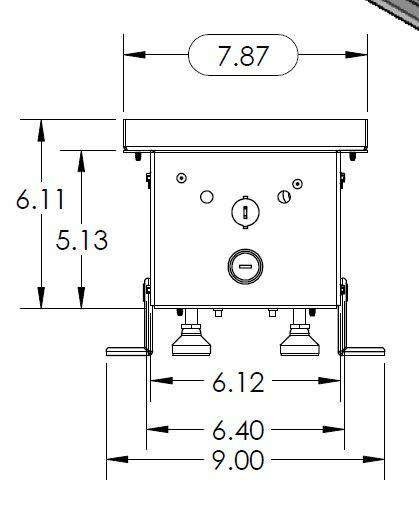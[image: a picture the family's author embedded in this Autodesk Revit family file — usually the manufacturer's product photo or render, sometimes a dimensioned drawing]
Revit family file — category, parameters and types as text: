
# Revit family: Convection_Heater-Berko-THX
name_source: partatom
category: Mechanical Equipment
revit_build: Autodesk Revit 2017 (Build: 20160225_1515(x64)
units: mm (PartAtom-declared; Revit-internal decimal feet)

## family parameters
Cut with Voids When Loaded = No
Host = Face
OmniClass Number = 23.75.70.17.14
OmniClass Title = Convectors
Part Type = Normal
Room Calculation Point = No
Round Connector Dimension = Use Diameter
Shared = No

## types (16) — shared parameters
Amps = 1 A
Apparent Load = 0 VA
Casing = Metal - Berko - Paint - Aluminum
Default Elevation = 3"
Description = THX Trench Heater
Frequency = 60 Hz
Height = 6"
Manufacturer = Berko
Number of Poles = 1
Phase = 2
Power Factor = 1
Product Name = THX Trench Heater
Product Page URL = https://www.marleymep.com
Surface Mount = No
URL = http://www.marleymep.com
Width = 3 5/8"

## per-type parameters (varying)
| type | Length | Length Constraint | Material | Model | Voltage | Watts |
| THX 2' 02188 208V | 2' - 0" | 2' - 4" |  | THX 2' 02188 | 208 V | 400 W |
| THX 3' 03188 208V | 3' - 0" | 3' - 0" |  | THX 3' 03188 | 208 V | 564 W |
| THX 4' 04188 208V | 4' - 0" | 4' - 0" |  | THX 4' 04188 | 208 V | 752 W |
| THX 5' 05188 208V | 5' - 0" | 5' - 0" |  | THX 5' 05188 | 208 V | 940 W |
| THX 2' 02250 208V | 2' - 0" | 2' - 4" |  | THX 2' 02250 | 208 V | 500 W |
| THX 3' 03250 208V | 3' - 0" | 3' - 0" | Metal - Berko - Paint - Aluminum | THX 3' 03250 | 208 V | 750 W |
| THX 4' 04250 208V | 4' - 0" | 4' - 0" |  | THX 4' 04250 | 208 V | 1000 W |
| THX 5' 05250 208V | 5' - 0" | 5' - 0" |  | THX 5' 05250 | 208 V | 1250 W |
| THX 2' 02188 277V | 2' - 0" | 2' - 4" |  | THX 2' 02188 | 277 V | 400 W |
| THX 2' 02250 277V | 2' - 0" | 2' - 4" |  | THX 2' 02250 | 277 V | 500 W |
| THX 3' 03188 277V | 3' - 0" | 3' - 0" |  | THX 3' 03188 | 277 V | 564 W |
| THX 3' 03250 277V | 3' - 0" | 3' - 0" | Metal - Berko - Paint - Aluminum | THX 3' 03250 | 277 V | 750 W |
| THX 4' 04188 277V | 4' - 0" | 4' - 0" |  | THX 4' 04188 | 277 V | 752 W |
| THX 4' 04250 277V | 4' - 0" | 4' - 0" |  | THX 4' 04250 | 277 V | 1000 W |
| THX 5' 05188 277V | 5' - 0" | 5' - 0" |  | THX 5' 05188 | 277 V | 940 W |
| THX 5' 05250 277V | 5' - 0" | 5' - 0" |  | THX 5' 05250 | 277 V | 1250 W |

## geometry (parser evidence)
native form markers: Blend x2, Sweep x1
no freeform markers — native parametric forms only
